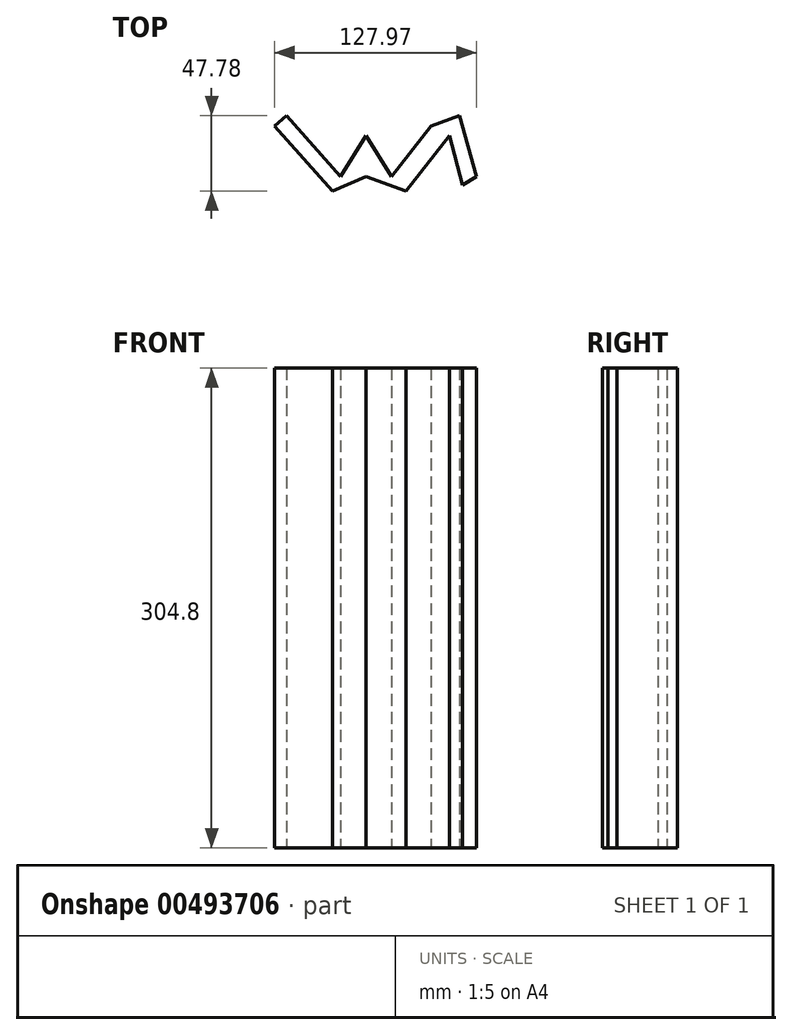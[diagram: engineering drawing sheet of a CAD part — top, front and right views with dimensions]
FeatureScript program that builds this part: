
annotation { "Feature Type Name" : "Feature", "Feature Type Description" : "" }
export const myFeature = defineFeature(function(context is Context, id is Id, definition is map)
    precondition{}
    {
        {
            var Q0;
            Q0=qCreatedBy(makeId("Top.planeOp"),FACE);
            var sketch = newSketch(context, id + "F0", { "sketchPlane" : qUnion([Q0])});
            skLineSegment(sketch, "E0", {"start": v(-69.65, 49.8) * mm, "end": v(-32.97, 8.54) * mm});
            skLineSegment(sketch, "E1", {"start": v(-69.65, 49.8) * mm, "end": v(-62.33, 56.32) * mm});
            skLineSegment(sketch, "E2", {"start": v(-62.33, 56.32) * mm, "end": v(-28.04, 17.75) * mm});
            skLineSegment(sketch, "E3", {"start": v(-28.04, 17.75) * mm, "end": v(-11.7, 43.78) * mm});
            skLineSegment(sketch, "E4", {"start": v(-11.7, 43.78) * mm, "end": v(4.53, 17.75) * mm});
            skLineSegment(sketch, "E5", {"start": v(4.53, 17.75) * mm, "end": v(29.57, 49.8) * mm});
            skLineSegment(sketch, "E6", {"start": v(-32.97, 8.54) * mm, "end": v(-11.7, 17.75) * mm});
            skLineSegment(sketch, "E7", {"start": v(-11.7, 17.75) * mm, "end": v(13.73, 8.54) * mm});
            skLineSegment(sketch, "E8", {"start": v(13.73, 8.54) * mm, "end": v(41.24, 43.78) * mm});
            skLineSegment(sketch, "E9", {"start": v(41.24, 43.78) * mm, "end": v(49.5, 12.25) * mm});
            skLineSegment(sketch, "E10", {"start": v(29.57, 49.8) * mm, "end": v(47.81, 56.32) * mm});
            skLineSegment(sketch, "E11", {"start": v(47.81, 56.32) * mm, "end": v(58.32, 17.75) * mm});
            skLineSegment(sketch, "E12", {"start": v(49.5, 12.25) * mm, "end": v(58.32, 17.75) * mm});
            skSolve(sketch);
        }
        {
            var Q0;
            Q0=makeQuery(id+"F0.imprint","IMPRINT",FACE,{"disambiguationData":[TD([[makeQuery(id+"F0.imprint","IMPRINT",EDGE,{"derivedFrom":sQuery(id+"F0.wireOp",EDGE,"E0")}),1.0]])]});
            extrude(context, id + "F1", {"entities" : qUnion([Q0]), "depth" : 304.8 * mm});
        }
    });
